# Revit family: 94022
name_source: partatom
category: Modelos genéricos
revit_build: Autodesk Revit 2016 (Build: 20150220_1215(x64)
units: mm (PartAtom-declared; Revit-internal decimal feet)

## family parameters
Com base no plano de trabalho = Não
Compartilhado = Não
Corte com vazios quando carregados = Não
Cota do conector redondo = Utilizar diâmetro
Pode hospedar o vergalhão = Não
Ponto de cálculo do ambiente = Não
Sempre na vertical = Sim
Tipo de parte = Normal

## types (1)
- 94024-203 CUBA RETANGULAR 56 X 34
    Comentários de tipos = Ler Manual de Instalação
    Código de montagem = 94024-203 CUBA RETANGULAR 56 X 34
    Descrição = 94024-203 CUBA RETANGULAR 56 X 34
    Desenvolvedor = Factory Cursos & Desenvolvimento
    Diametro = 48  [stored 0.15748 ft]
    Dimensões (mm) = 590X370 (dim ext.)
    Fabricante = Tramontina
    Modelo = 94024-203 CUBA RETANGULAR 56 X 34
    Site do desenvolvedor = www.factorycursos.com.br
    Tipo de imagem = 94024203_1.jpg
    URL = www.tramontina.com.br

note: [stored X ft] marks values corroborated as IEEE doubles in the binary element streams (Revit-internal decimal feet)
